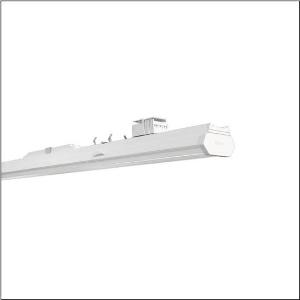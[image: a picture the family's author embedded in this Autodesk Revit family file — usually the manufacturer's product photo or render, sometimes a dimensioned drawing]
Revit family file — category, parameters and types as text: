
# Revit family: licross_r__21_protected_mo_52td12dn4a5g3s4_b622
name_source: partatom
category: Lighting Fixtures
units: mm (PartAtom-declared; Revit-internal decimal feet)

## family parameters
Cut with Voids When Loaded = No
Host = Face
Light Source = No
Part Type = Normal
Room Calculation Point = No
Round Connector Dimension = Use Diameter
Shared = No

## types (1)
- --- (1 x LED, 940 lm, 6.8 W, 4000K)
    Apparent Load = 7 VA
    CIE Flux Codes = 73 92 98 99 100
    Color Rendering = 80
    Color Temperature = 4000K
    Default Elevation = 1800 mm
    Description = Licross® 21 Protected MO, luminaire insert, of sheet steel, galvanised, coil coated, white, length: 1.500mm, width: 90mm, height: 103mm, LED rated luminous flux: 10.700lm, light colour: 840, control gear: DALI 2, with plug, 6-pole, with phase selection, for trunking rail, 9 or 11-core, mains connection: 220..240V, AC, 50/60Hz, rated input power: 66W, for trunking rail, 9-/11-core, halogen-free wiring, for emergency light function, converter,control gear: single battery element, battery: LiFeP04, 9Ah, primary light control with lens, of plastic, primary optical cover: cover, of PMMA, light emission: direct distribution, primary light characteristic: symmetric, protection rating (complete): IP54, insulation class (complete): insulation class I (protective earthing), certification: CE, UKCA, protection symbol: D if used in an environment with non-conductive dust loads with corresponding accessories, impact resistance: IK06, permissible ambient temperature for indoor applications: +5..+35°C, standard: EN 60598-2-22, LABS conformity tested according to VDMA 24364:2018-05, reducing of maximum allowable ambient temperature of 5°C with ceiling mounting, corresponds to IFS (International Featured Standards) requirements for safety and quality in the food industry, packaging unit: 1 piece
    Height = 92 mm
    Lamp = 1 x LED
    Lamp Light Flux = 940 lm
    Lamp Power = 6.8 W
    Lamp count = 1
    Length = 1500 mm
    Luminous efficacy = 138 lm/W
    Manufacturer = Siteco
    ModVariant = No
    Model = 52TD12DN4A5G3S4
    Mounting Place = Ceiling
    Mounting Type = Pendant
    Number of Poles = 1
    OnlyDefault = Yes
    Power Factor = 1
    Product Name = Licross® 21 Protected MO
    Product group = luminaire insert
    ProductGroupID = 901
    Protection Class = Protection class I
    Protection Degree = IP 54
    RLX_Detail_Level = 1
    RLX_Emergency_Light_Flux = 0 lm
    RLX_Emergency_Type = 0
    RLX_Emergency_Type_DB = No
    RlxData = <blob elided: 24901 chars, md5=d8f44b88>
    Socket = socket
    Standby Power = 0 W
    System Light Flux = 940 lm
    System Power = 7 W
    Type Comments = : emergency light operation: 3 h
    Type Image = l_1256148.jpg
    URL = http://relux.com
    VarID = @adj_041011
    Voltage = 0 V
    Weight = 0.00 kg
    Width = 88 mm

## geometry (parser evidence)
native form markers: Blend x4, Sweep x12
no freeform markers — native parametric forms only
